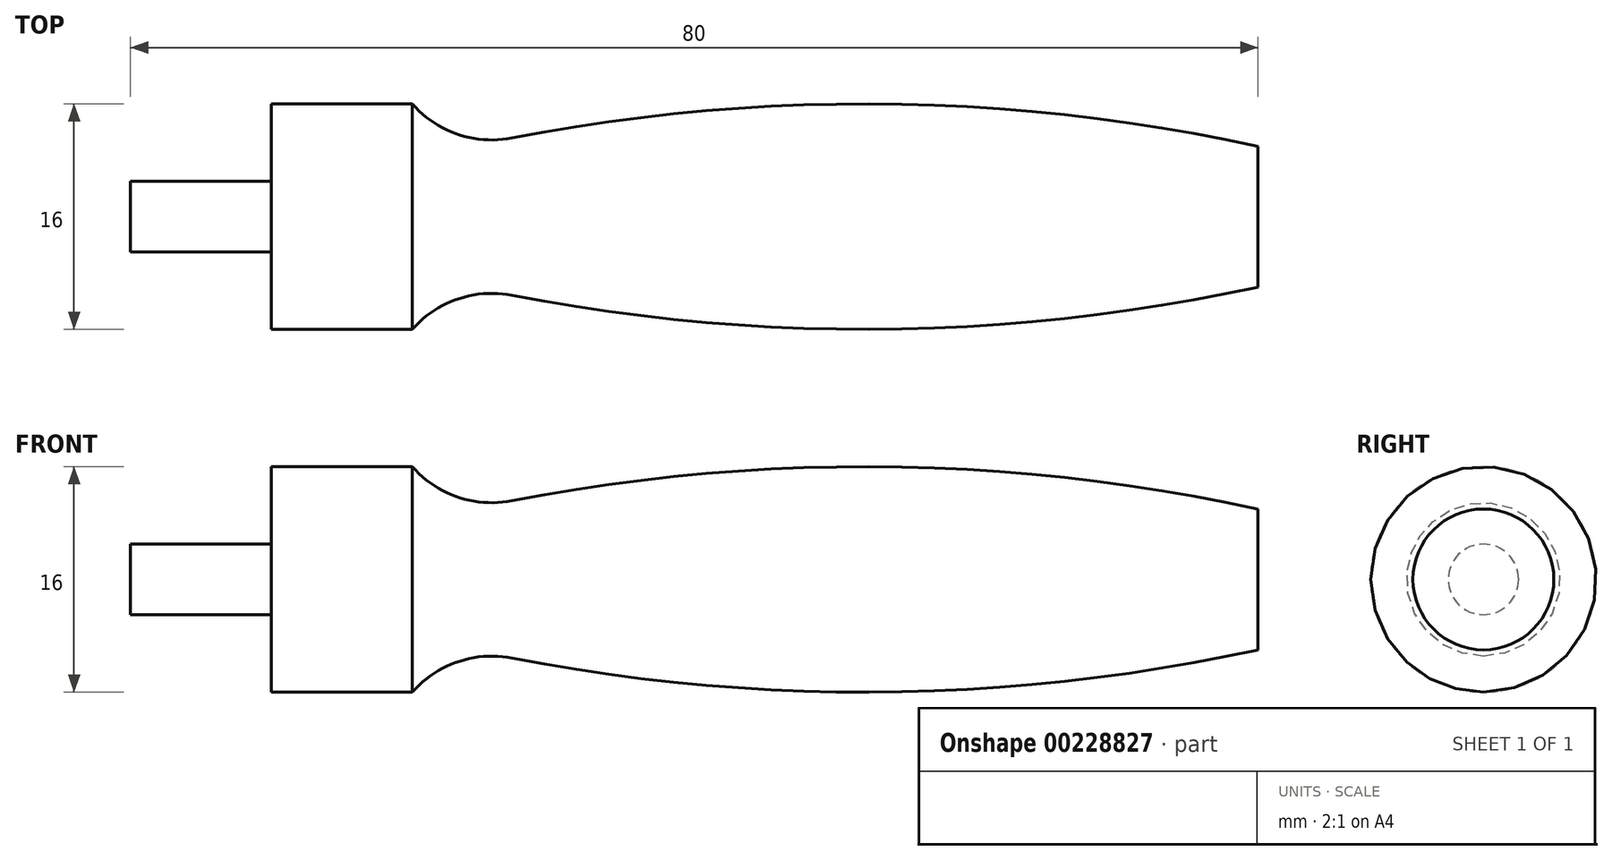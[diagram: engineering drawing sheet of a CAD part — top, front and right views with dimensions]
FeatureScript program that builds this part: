
annotation { "Feature Type Name" : "Feature", "Feature Type Description" : "" }
export const myFeature = defineFeature(function(context is Context, id is Id, definition is map)
    precondition{}
    {
        {
            var Q0;
            Q0=qCreatedBy(makeId("Front.planeOp"),FACE);
            var sketch = newSketch(context, id + "F0", { "sketchPlane" : qUnion([Q0])});
            skLineSegment(sketch, "E0.bottom", {"start": v(-10, 2.5) * mm, "end": v(0, 2.5) * mm});
            skLineSegment(sketch, "E0.top", {"start": v(-10, 0) * mm, "end": v(0, 0) * mm});
            skLineSegment(sketch, "E0.left", {"start": v(-10, 2.5) * mm, "end": v(-10, 0) * mm});
            skLineSegment(sketch, "E0.right", {"start": v(0, 2.5) * mm, "end": v(0, 0) * mm});
            skLineSegment(sketch, "E1.bottom", {"start": v(0, 8) * mm, "end": v(10, 8) * mm});
            skLineSegment(sketch, "E1.top", {"start": v(0, 0) * mm, "end": v(10, 0) * mm});
            skLineSegment(sketch, "E1.left", {"start": v(0, 8) * mm, "end": v(0, 0) * mm});
            skLineSegment(sketch, "E1.right", {"start": v(10, 8) * mm, "end": v(10, 0) * mm});
            skLineSegment(sketch, "E2", {"start": v(10, 0) * mm, "end": v(70, 0) * mm});
            skLineSegment(sketch, "E3", {"start": v(70, 5) * mm, "end": v(70, 0) * mm});
            skArc(sketch, "E4", {"start": v(70, 5) * mm, "mid": v(39.94, 7.98) * mm, "end": v(10, 4) * mm});
            skSolve(sketch);
        }
        {
            var Q0;
            {var subQ0=sQuery(id+"F0.wireOp",EDGE,"E0.bottom");Q0=makeQuery(id+"F0.imprint","IMPRINT",FACE,{"disambiguationData":[TD([[makeQuery(id+"F0.imprint","IMPRINT",EDGE,{"derivedFrom":subQ0}),-1.0]])]});}
            var Q1;
            {var subQ3=sQuery(id+"F0.wireOp",EDGE,"E1.bottom");Q1=makeQuery(id+"F0.imprint","IMPRINT",FACE,{"disambiguationData":[TD([[makeQuery(id+"F0.imprint","IMPRINT",EDGE,{"derivedFrom":subQ3}),-1.0]])]});}
            var Q2;
            {var subQ0=sQuery(id+"F0.wireOp",EDGE,"E2");Q2=makeQuery(id+"F0.imprint","IMPRINT",FACE,{"disambiguationData":[TD([[makeQuery(id+"F0.imprint","IMPRINT",EDGE,{"derivedFrom":subQ0}),1.0]])]});}
            var Q3;
            Q3=sQuery(id+"F0.wireOp",EDGE,"E2");
            revolve(context, id + "F1", {"entities" : qUnion([Q0, Q1, Q2]), "axis" : qUnion([Q3]), "revolveType" : RevolveType.FULL});
        }
        {
            var Q0;
            Q0=makeQuery(id+"F1.opRevolve","SWEPT_EDGE",EDGE,{"disambiguationData":[OSD([sQuery(id+"F0.wireOp",EDGE,"E1.right"),sQuery(id+"F0.wireOp",EDGE,"E4")])]});
            fillet(context, id + "F2", {"entities" : qUnion([Q0]), "radius" : 7.5 * mm, "tangentPropagation" : true, "allowEdgeOverflow" : false});
        }
    });
